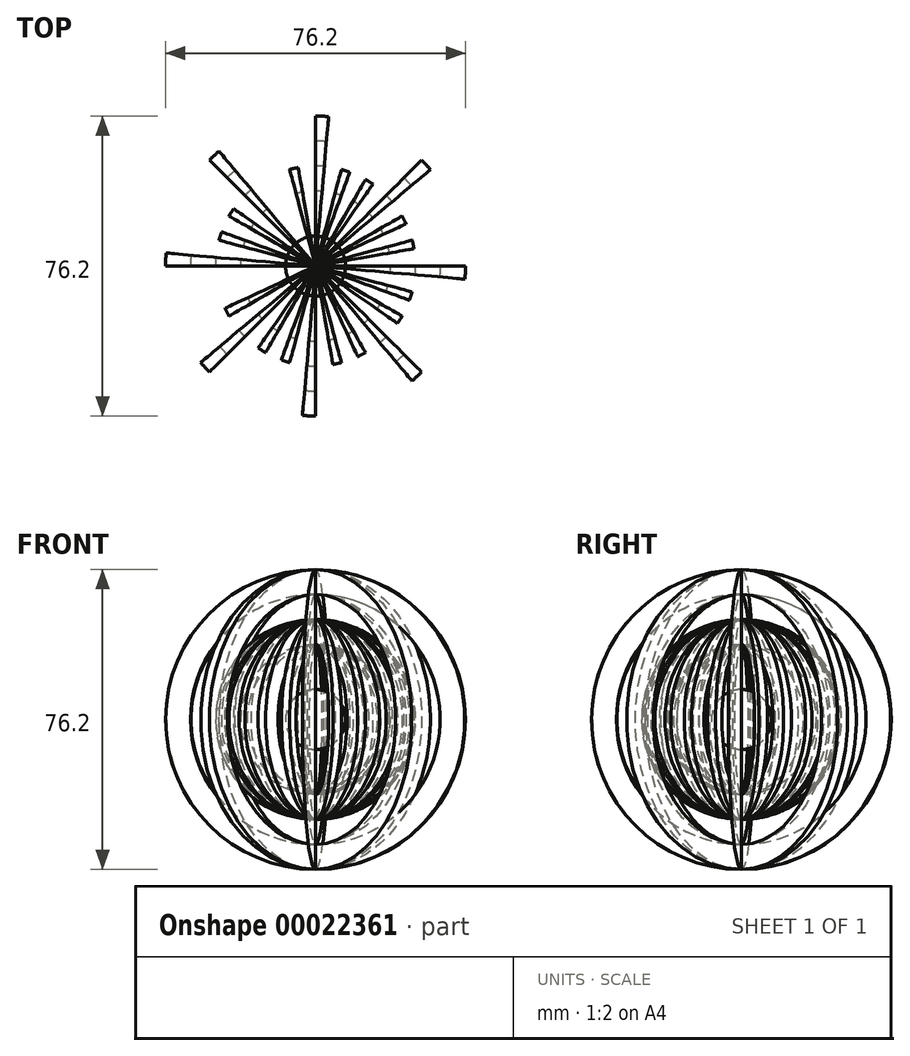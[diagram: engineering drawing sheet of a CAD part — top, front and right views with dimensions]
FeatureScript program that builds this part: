
annotation { "Feature Type Name" : "Feature", "Feature Type Description" : "" }
export const myFeature = defineFeature(function(context is Context, id is Id, definition is map)
    precondition{}
    {
        {
            var Q0;
            Q0=qCreatedBy(makeId("Right.planeOp"),FACE);
            var sketch = newSketch(context, id + "F0", { "sketchPlane" : qUnion([Q0])});
            skCircle(sketch, "E0", {"center": v(0, 0) * mm, "radius": 12.9 * mm});
            skCircle(sketch, "E1", {"center": v(0, 0) * mm, "radius": 6.75 * mm});
            skCircle(sketch, "E2", {"center": v(0, 0) * mm, "radius": 19.05 * mm});
            skCircle(sketch, "E3", {"center": v(0, 0) * mm, "radius": 25.4 * mm});
            skLineSegment(sketch, "E4", {"start": v(0, 49.46) * mm, "end": v(0, -44.6) * mm});
            skCircle(sketch, "E5", {"center": v(0, 0) * mm, "radius": 30.75 * mm});
            skLineSegment(sketch, "E6", {"start": v(0, 49.46) * mm, "end": v(0, 76.29) * mm, "construction": true});
            skLineSegment(sketch, "E7", {"start": v(0, 76.29) * mm, "end": v(7.81, 69.76) * mm, "construction": true});
            skLineSegment(sketch, "E8", {"start": v(-75.09, 75.98) * mm, "end": v(75.64, 76.29) * mm});
            skSolve(sketch);
        }
        {
            var Q0;
            {var subQ0=sQuery(id+"F0.wireOp",EDGE,"E4");var subQ1=sQuery(id+"F0.wireOp",EDGE,"E1");var subQ3=makeQuery(id+"F0.imprint","INTERSECT",VERTEX,{"disambiguationData":[OD(0.0)],"derivedFrom":[subQ1,subQ0]});Q0=makeQuery(id+"F0.imprint","IMPRINT",FACE,{"disambiguationData":[TD([[makeQuery(id+"F0.imprint","IMPRINT",EDGE,{"disambiguationData":[TD([[subQ3,1.0]])],"derivedFrom":subQ1}),1.0]])]});}
            var Q1;
            Q1=sQuery(id+"F0.wireOp",EDGE,"E4");
            revolve(context, id + "F1", {"entities" : qUnion([Q0]), "axis" : qUnion([Q1]), "revolveType" : RevolveType.FULL});
        }
        {
            var Q0;
            {var subQ0=sQuery(id+"F0.wireOp",EDGE,"E4");var subQ3=sQuery(id+"F0.wireOp",EDGE,"E2");var subQ6=makeQuery(id+"F0.imprint","INTERSECT",VERTEX,{"disambiguationData":[OD(0.0)],"derivedFrom":[subQ3,subQ0]});Q0=makeQuery(id+"F0.imprint","IMPRINT",FACE,{"disambiguationData":[TD([[makeQuery(id+"F0.imprint","IMPRINT",EDGE,{"disambiguationData":[TD([[subQ6,1.0]])],"derivedFrom":subQ3}),-1.0]])]});}
            var Q1;
            Q1=sQuery(id+"F0.wireOp",EDGE,"E4");
            revolve(context, id + "F2", {"entities" : qUnion([Q0]), "axis" : qUnion([Q1]), "revolveType" : RevolveType.ONE_DIRECTION, "angle" : 5 * degree});
        }
        {
            var Q0;
            Q0=qCreatedBy(makeId("Front.planeOp"),FACE);
            var sketch = newSketch(context, id + "F3", { "sketchPlane" : qUnion([Q0])});
            skCircle(sketch, "E9", {"center": v(0, 0) * mm, "radius": 25.4 * mm});
            skCircle(sketch, "E10", {"center": v(0, 0) * mm, "radius": 19.05 * mm});
            skLineSegment(sketch, "E11", {"start": v(0, 49.68) * mm, "end": v(0, -45.03) * mm});
            skLineSegment(sketch, "E12", {"start": v(77.84, 77.44) * mm, "end": v(-74.78, 77.44) * mm});
            skSolve(sketch);
        }
        {
            var Q0;
            {var subQ0=sQuery(id+"F3.wireOp",EDGE,"E11");var subQ3=sQuery(id+"F3.wireOp",EDGE,"E9");var subQ6=makeQuery(id+"F3.imprint","INTERSECT",VERTEX,{"disambiguationData":[OD(0.0)],"derivedFrom":[subQ3,subQ0]});Q0=makeQuery(id+"F3.imprint","IMPRINT",FACE,{"disambiguationData":[TD([[makeQuery(id+"F3.imprint","IMPRINT",EDGE,{"disambiguationData":[TD([[subQ6,-1.0]])],"derivedFrom":subQ3}),1.0]])]});}
            var Q1;
            Q1=sQuery(id+"F3.wireOp",EDGE,"E11");
            revolve(context, id + "F4", {"entities" : qUnion([Q0]), "axis" : qUnion([Q1]), "revolveType" : RevolveType.ONE_DIRECTION, "angle" : 5 * degree});
        }
        {
            var Q0;
            {var subQ0=sQuery(id+"F3.wireOp",EDGE,"E11");var subQ3=sQuery(id+"F3.wireOp",EDGE,"E9");var subQ6=makeQuery(id+"F3.imprint","INTERSECT",VERTEX,{"disambiguationData":[OD(0.0)],"derivedFrom":[subQ3,subQ0]});Q0=makeQuery(id+"F3.imprint","IMPRINT",FACE,{"disambiguationData":[TD([[makeQuery(id+"F3.imprint","IMPRINT",EDGE,{"disambiguationData":[TD([[subQ6,1.0]])],"derivedFrom":subQ3}),1.0]])]});}
            var Q1;
            Q1=sQuery(id+"F3.wireOp",EDGE,"E11");
            revolve(context, id + "F5", {"entities" : qUnion([Q0]), "axis" : qUnion([Q1]), "revolveType" : RevolveType.ONE_DIRECTION, "angle" : 5 * degree});
        }
        {
            var Q0;
            Q0=sQuery(id+"F3.wireOp",EDGE,"E11");
            cPlane(context, id + "F6", {"entities" : qUnion([Q0]), "cplaneType" : CPlaneType.LINE_ANGLE, "offset" : 152.4 * mm, "angle" : 135 * degree, "width" : 152.4 * mm, "height" : 152.4 * mm});
        }
        {
            var Q0;
            Q0=qCreatedBy(id+"F6.planeOp",FACE);
            var sketch = newSketch(context, id + "F7", { "sketchPlane" : qUnion([Q0])});
            skCircle(sketch, "E13", {"center": v(0, 0) * mm, "radius": 25.4 * mm});
            skCircle(sketch, "E14", {"center": v(0, 0) * mm, "radius": 19.05 * mm});
            skLineSegment(sketch, "E15", {"start": v(0, 49) * mm, "end": v(0, -46.81) * mm});
            skSolve(sketch);
        }
        {
            var Q0;
            {var subQ0=sQuery(id+"F7.wireOp",EDGE,"E15");var subQ3=sQuery(id+"F7.wireOp",EDGE,"E13");var subQ6=makeQuery(id+"F7.imprint","INTERSECT",VERTEX,{"disambiguationData":[OD(0.0)],"derivedFrom":[subQ3,subQ0]});Q0=makeQuery(id+"F7.imprint","IMPRINT",FACE,{"disambiguationData":[TD([[makeQuery(id+"F7.imprint","IMPRINT",EDGE,{"disambiguationData":[TD([[subQ6,1.0]])],"derivedFrom":subQ3}),1.0]])]});}
            var Q1;
            Q1=sQuery(id+"F7.wireOp",EDGE,"E15");
            revolve(context, id + "F8", {"entities" : qUnion([Q0]), "axis" : qUnion([Q1]), "revolveType" : RevolveType.ONE_DIRECTION, "angle" : 5 * degree});
        }
        {
            var Q0;
            {var subQ0=sQuery(id+"F7.wireOp",EDGE,"E15");var subQ3=sQuery(id+"F7.wireOp",EDGE,"E13");var subQ6=makeQuery(id+"F7.imprint","INTERSECT",VERTEX,{"disambiguationData":[OD(0.0)],"derivedFrom":[subQ3,subQ0]});Q0=makeQuery(id+"F7.imprint","IMPRINT",FACE,{"disambiguationData":[TD([[makeQuery(id+"F7.imprint","IMPRINT",EDGE,{"disambiguationData":[TD([[subQ6,-1.0]])],"derivedFrom":subQ3}),1.0]])]});}
            var Q1;
            Q1=sQuery(id+"F7.wireOp",EDGE,"E15");
            revolve(context, id + "F9", {"entities" : qUnion([Q0]), "axis" : qUnion([Q1]), "revolveType" : RevolveType.ONE_DIRECTION, "angle" : 5 * degree});
        }
        {
            var Q0;
            Q0=sQuery(id+"F7.wireOp",EDGE,"E15");
            cPlane(context, id + "F10", {"entities" : qUnion([Q0]), "cplaneType" : CPlaneType.LINE_ANGLE, "offset" : 152.4 * mm, "angle" : 45 * degree, "width" : 152.4 * mm, "height" : 152.4 * mm});
        }
        {
            var Q0;
            Q0=qCreatedBy(id+"F10.planeOp",FACE);
            var sketch = newSketch(context, id + "F11", { "sketchPlane" : qUnion([Q0])});
            skCircle(sketch, "E16", {"center": v(0, 0) * mm, "radius": 19.05 * mm});
            skLineSegment(sketch, "E17", {"start": v(0, 49.08) * mm, "end": v(0, -50.96) * mm});
            skCircle(sketch, "E18", {"center": v(0, 0) * mm, "radius": 25.4 * mm});
            skSolve(sketch);
        }
        {
            var Q0;
            {var subQ1=sQuery(id+"F11.wireOp",EDGE,"E17");var subQ4=sQuery(id+"F11.wireOp",EDGE,"E16");var subQ6=makeQuery(id+"F11.imprint","INTERSECT",VERTEX,{"disambiguationData":[OD(0.0)],"derivedFrom":[subQ4,subQ1]});Q0=makeQuery(id+"F11.imprint","IMPRINT",FACE,{"disambiguationData":[TD([[makeQuery(id+"F11.imprint","IMPRINT",EDGE,{"disambiguationData":[TD([[subQ6,1.0]])],"derivedFrom":subQ4}),-1.0]])]});}
            var Q1;
            Q1=sQuery(id+"F11.wireOp",EDGE,"E17");
            revolve(context, id + "F12", {"entities" : qUnion([Q0]), "axis" : qUnion([Q1]), "revolveType" : RevolveType.ONE_DIRECTION, "angle" : 5 * degree});
        }
        {
            var Q0;
            {var subQ0=sQuery(id+"F11.wireOp",EDGE,"E17");var subQ1=sQuery(id+"F11.wireOp",EDGE,"E16");var subQ6=makeQuery(id+"F11.imprint","INTERSECT",VERTEX,{"disambiguationData":[OD(0.0)],"derivedFrom":[subQ1,subQ0]});Q0=makeQuery(id+"F11.imprint","IMPRINT",FACE,{"disambiguationData":[TD([[makeQuery(id+"F11.imprint","IMPRINT",EDGE,{"disambiguationData":[TD([[subQ6,-1.0]])],"derivedFrom":subQ1}),-1.0]])]});}
            var Q1;
            Q1=sQuery(id+"F11.wireOp",EDGE,"E17");
            revolve(context, id + "F13", {"entities" : qUnion([Q0]), "axis" : qUnion([Q1]), "revolveType" : RevolveType.ONE_DIRECTION, "angle" : 5 * degree});
        }
        {
            var Q0;
            Q0=sQuery(id+"F11.wireOp",EDGE,"E17");
            cPlane(context, id + "F14", {"entities" : qUnion([Q0]), "cplaneType" : CPlaneType.LINE_ANGLE, "offset" : 152.4 * mm, "angle" : 15 * degree, "width" : 152.4 * mm, "height" : 152.4 * mm});
        }
        {
            var Q0;
            Q0=qCreatedBy(id+"F14.planeOp",FACE);
            var sketch = newSketch(context, id + "F15", { "sketchPlane" : qUnion([Q0])});
            skArc(sketch, "E19", {"start": v(0, 25.4) * mm, "mid": v(-25.4, 0) * mm, "end": v(0, -25.4) * mm});
            skArc(sketch, "E20", {"start": v(0, 19.05) * mm, "mid": v(-19.05, 0) * mm, "end": v(0, -19.05) * mm});
            skLineSegment(sketch, "E21", {"start": v(0, 47.4) * mm, "end": v(0, -52.09) * mm});
            skSolve(sketch);
        }
        {
            var Q0;
            {var subQ2=sQuery(id+"F15.wireOp",EDGE,"E19");Q0=makeQuery(id+"F15.imprint","IMPRINT",FACE,{"disambiguationData":[TD([[makeQuery(id+"F15.imprint","IMPRINT",EDGE,{"derivedFrom":subQ2}),1.0]])]});}
            var Q1;
            Q1=sQuery(id+"F15.wireOp",EDGE,"E21");
            revolve(context, id + "F16", {"entities" : qUnion([Q0]), "axis" : qUnion([Q1]), "revolveType" : RevolveType.ONE_DIRECTION, "angle" : 5 * degree});
        }
        {
            var Q0;
            Q0=qCreatedBy(id+"F14.planeOp",FACE);
            var sketch = newSketch(context, id + "F17", { "sketchPlane" : qUnion([Q0])});
            skArc(sketch, "E22", {"start": v(0, -25.4) * mm, "mid": v(25.4, 0) * mm, "end": v(0, 25.4) * mm});
            skArc(sketch, "E23", {"start": v(0, -19.05) * mm, "mid": v(19.05, 0) * mm, "end": v(0, 19.05) * mm});
            skLineSegment(sketch, "E24", {"start": v(0, 48.59) * mm, "end": v(0, -48.7) * mm});
            skSolve(sketch);
        }
        {
            var Q0;
            {var subQ2=sQuery(id+"F17.wireOp",EDGE,"E22");Q0=makeQuery(id+"F17.imprint","IMPRINT",FACE,{"disambiguationData":[TD([[makeQuery(id+"F17.imprint","IMPRINT",EDGE,{"derivedFrom":subQ2}),1.0]])]});}
            var Q1;
            Q1=sQuery(id+"F17.wireOp",EDGE,"E24");
            revolve(context, id + "F18", {"entities" : qUnion([Q0]), "axis" : qUnion([Q1]), "revolveType" : RevolveType.ONE_DIRECTION, "angle" : 5 * degree});
        }
        {
            var Q0;
            Q0=sQuery(id+"F11.wireOp",EDGE,"E17");
            cPlane(context, id + "F19", {"entities" : qUnion([Q0]), "cplaneType" : CPlaneType.LINE_ANGLE, "offset" : 152.4 * mm, "angle" : 30 * degree, "width" : 152.4 * mm, "height" : 152.4 * mm});
        }
        {
            var Q0;
            Q0=qCreatedBy(id+"F19.planeOp",FACE);
            var sketch = newSketch(context, id + "F20", { "sketchPlane" : qUnion([Q0])});
            skArc(sketch, "E25", {"start": v(0, -25.4) * mm, "mid": v(25.4, 0) * mm, "end": v(0, 25.4) * mm});
            skArc(sketch, "E26", {"start": v(0, -19.05) * mm, "mid": v(19.05, 0) * mm, "end": v(0, 19.05) * mm});
            skLineSegment(sketch, "E27", {"start": v(0, 48.62) * mm, "end": v(0, -52.83) * mm});
            skSolve(sketch);
        }
        {
            var Q0;
            {var subQ2=sQuery(id+"F20.wireOp",EDGE,"E25");Q0=makeQuery(id+"F20.imprint","IMPRINT",FACE,{"disambiguationData":[TD([[makeQuery(id+"F20.imprint","IMPRINT",EDGE,{"derivedFrom":subQ2}),1.0]])]});}
            var Q1;
            Q1=sQuery(id+"F20.wireOp",EDGE,"E27");
            revolve(context, id + "F21", {"operationType" : NewBodyOperationType.ADD, "entities" : qUnion([Q0]), "axis" : qUnion([Q1]), "revolveType" : RevolveType.ONE_DIRECTION, "angle" : 5 * degree});
        }
        {
            var Q0;
            Q0=qCreatedBy(id+"F19.planeOp",FACE);
            var sketch = newSketch(context, id + "F22", { "sketchPlane" : qUnion([Q0])});
            skArc(sketch, "E28", {"start": v(0, 25.4) * mm, "mid": v(-25.4, 0) * mm, "end": v(0, -25.4) * mm});
            skArc(sketch, "E29", {"start": v(0, 19.05) * mm, "mid": v(-19.05, 0) * mm, "end": v(0, -19.05) * mm});
            skLineSegment(sketch, "E30", {"start": v(0, 50.56) * mm, "end": v(0, -52.17) * mm});
            skSolve(sketch);
        }
        {
            var Q0;
            {var subQ2=sQuery(id+"F22.wireOp",EDGE,"E28");Q0=makeQuery(id+"F22.imprint","IMPRINT",FACE,{"disambiguationData":[TD([[makeQuery(id+"F22.imprint","IMPRINT",EDGE,{"derivedFrom":subQ2}),1.0]])]});}
            var Q1;
            Q1=sQuery(id+"F22.wireOp",EDGE,"E30");
            revolve(context, id + "F23", {"operationType" : NewBodyOperationType.ADD, "entities" : qUnion([Q0]), "axis" : qUnion([Q1]), "revolveType" : RevolveType.ONE_DIRECTION, "angle" : 5 * degree});
        }
        {
            var Q0;
            Q0=sQuery(id+"F11.wireOp",EDGE,"E17");
            cPlane(context, id + "F24", {"entities" : qUnion([Q0]), "cplaneType" : CPlaneType.LINE_ANGLE, "offset" : 152.4 * mm, "angle" : 60 * degree, "width" : 152.4 * mm, "height" : 152.4 * mm});
        }
        {
            var Q0;
            Q0=qCreatedBy(id+"F24.planeOp",FACE);
            var sketch = newSketch(context, id + "F25", { "sketchPlane" : qUnion([Q0])});
            skCircle(sketch, "E31", {"center": v(0, 0) * mm, "radius": 25.4 * mm});
            skCircle(sketch, "E32", {"center": v(0, 0) * mm, "radius": 19.05 * mm});
            skLineSegment(sketch, "E33", {"start": v(0, 47.75) * mm, "end": v(0, -47.16) * mm});
            skSolve(sketch);
        }
        {
            var Q0;
            {var subQ0=sQuery(id+"F25.wireOp",EDGE,"E33");var subQ3=sQuery(id+"F25.wireOp",EDGE,"E31");var subQ6=makeQuery(id+"F25.imprint","INTERSECT",VERTEX,{"disambiguationData":[OD(0.0)],"derivedFrom":[subQ3,subQ0]});Q0=makeQuery(id+"F25.imprint","IMPRINT",FACE,{"disambiguationData":[TD([[makeQuery(id+"F25.imprint","IMPRINT",EDGE,{"disambiguationData":[TD([[subQ6,1.0]])],"derivedFrom":subQ3}),1.0]])]});}
            var Q1;
            Q1=sQuery(id+"F25.wireOp",EDGE,"E33");
            revolve(context, id + "F26", {"operationType" : NewBodyOperationType.ADD, "entities" : qUnion([Q0]), "axis" : qUnion([Q1]), "revolveType" : RevolveType.ONE_DIRECTION, "angle" : 5 * degree});
        }
        {
            var Q0;
            {var subQ0=sQuery(id+"F25.wireOp",EDGE,"E33");var subQ3=sQuery(id+"F25.wireOp",EDGE,"E31");var subQ6=makeQuery(id+"F25.imprint","INTERSECT",VERTEX,{"disambiguationData":[OD(0.0)],"derivedFrom":[subQ3,subQ0]});Q0=makeQuery(id+"F25.imprint","IMPRINT",FACE,{"disambiguationData":[TD([[makeQuery(id+"F25.imprint","IMPRINT",EDGE,{"disambiguationData":[TD([[subQ6,-1.0]])],"derivedFrom":subQ3}),1.0]])]});}
            var Q1;
            Q1=sQuery(id+"F25.wireOp",EDGE,"E33");
            revolve(context, id + "F27", {"entities" : qUnion([Q0]), "axis" : qUnion([Q1]), "revolveType" : RevolveType.ONE_DIRECTION, "angle" : 5 * degree});
        }
        {
            var Q0;
            Q0=sQuery(id+"F25.wireOp",EDGE,"E33");
            cPlane(context, id + "F28", {"entities" : qUnion([Q0]), "cplaneType" : CPlaneType.LINE_ANGLE, "offset" : 152.4 * mm, "angle" : 75 * degree, "width" : 152.4 * mm, "height" : 152.4 * mm});
        }
        {
            var Q0;
            Q0=qCreatedBy(id+"F28.planeOp",FACE);
            var sketch = newSketch(context, id + "F29", { "sketchPlane" : qUnion([Q0])});
            skCircle(sketch, "E34", {"center": v(0, 0) * mm, "radius": 25.4 * mm});
            skCircle(sketch, "E35", {"center": v(0, 0) * mm, "radius": 19.05 * mm});
            skLineSegment(sketch, "E36", {"start": v(0, 25.4) * mm, "end": v(0, -25.4) * mm});
            skLineSegment(sketch, "E37", {"start": v(0, 39.45) * mm, "end": v(0, -34.84) * mm});
            skSolve(sketch);
        }
        {
            var Q0;
            {var subQ0=sQuery(id+"F29.wireOp",EDGE,"E37");var subQ3=sQuery(id+"F29.wireOp",EDGE,"E34");var subQ6=makeQuery(id+"F29.imprint","INTERSECT",VERTEX,{"disambiguationData":[OD(0.0)],"derivedFrom":[subQ3,subQ0]});Q0=makeQuery(id+"F29.imprint","IMPRINT",FACE,{"disambiguationData":[TD([[makeQuery(id+"F29.imprint","IMPRINT",EDGE,{"disambiguationData":[TD([[subQ6,1.0]])],"derivedFrom":subQ3}),1.0]])]});}
            var Q1;
            Q1=sQuery(id+"F29.wireOp",EDGE,"E36");
            revolve(context, id + "F30", {"operationType" : NewBodyOperationType.ADD, "entities" : qUnion([Q0]), "axis" : qUnion([Q1]), "revolveType" : RevolveType.ONE_DIRECTION, "angle" : 5 * degree});
        }
        {
            var Q0;
            Q0=qCreatedBy(id+"F28.planeOp",FACE);
            var sketch = newSketch(context, id + "F31", { "sketchPlane" : qUnion([Q0])});
            skArc(sketch, "E38", {"start": v(0, 25.4) * mm, "mid": v(-25.4, 0) * mm, "end": v(0, -25.4) * mm});
            skArc(sketch, "E39", {"start": v(0, 19.05) * mm, "mid": v(-19.05, 0) * mm, "end": v(0, -19.05) * mm});
            skLineSegment(sketch, "E40", {"start": v(0, 39.76) * mm, "end": v(0, -34.84) * mm});
            skSolve(sketch);
        }
        {
            var Q0;
            {var subQ2=sQuery(id+"F31.wireOp",EDGE,"E38");Q0=makeQuery(id+"F31.imprint","IMPRINT",FACE,{"disambiguationData":[TD([[makeQuery(id+"F31.imprint","IMPRINT",EDGE,{"derivedFrom":subQ2}),1.0]])]});}
            var Q1;
            Q1=sQuery(id+"F31.wireOp",EDGE,"E40");
            revolve(context, id + "F32", {"operationType" : NewBodyOperationType.ADD, "entities" : qUnion([Q0]), "axis" : qUnion([Q1]), "revolveType" : RevolveType.ONE_DIRECTION, "angle" : 5 * degree});
        }
        {
            var Q0;
            Q0=sQuery(id+"F29.wireOp",EDGE,"E37");
            cPlane(context, id + "F33", {"entities" : qUnion([Q0]), "cplaneType" : CPlaneType.LINE_ANGLE, "offset" : 152.4 * mm, "angle" : 105 * degree, "width" : 152.4 * mm, "height" : 152.4 * mm});
        }
        {
            var Q0;
            Q0=qCreatedBy(id+"F33.planeOp",FACE);
            var sketch = newSketch(context, id + "F34", { "sketchPlane" : qUnion([Q0])});
            skCircle(sketch, "E41", {"center": v(0, 0) * mm, "radius": 25.4 * mm});
            skCircle(sketch, "E42", {"center": v(0, 0) * mm, "radius": 19.05 * mm});
            skLineSegment(sketch, "E43", {"start": v(0, 30.33) * mm, "end": v(0, -31.57) * mm});
            skSolve(sketch);
        }
        {
            var Q0;
            {var subQ0=sQuery(id+"F34.wireOp",EDGE,"E43");var subQ3=sQuery(id+"F34.wireOp",EDGE,"E41");var subQ6=makeQuery(id+"F34.imprint","INTERSECT",VERTEX,{"disambiguationData":[OD(0.0)],"derivedFrom":[subQ3,subQ0]});Q0=makeQuery(id+"F34.imprint","IMPRINT",FACE,{"disambiguationData":[TD([[makeQuery(id+"F34.imprint","IMPRINT",EDGE,{"disambiguationData":[TD([[subQ6,1.0]])],"derivedFrom":subQ3}),1.0]])]});}
            var Q1;
            Q1=sQuery(id+"F34.wireOp",EDGE,"E43");
            revolve(context, id + "F35", {"entities" : qUnion([Q0]), "axis" : qUnion([Q1]), "revolveType" : RevolveType.ONE_DIRECTION, "angle" : 5 * degree});
        }
        {
            var Q0;
            {var subQ0=sQuery(id+"F34.wireOp",EDGE,"E43");var subQ3=sQuery(id+"F34.wireOp",EDGE,"E41");var subQ6=makeQuery(id+"F34.imprint","INTERSECT",VERTEX,{"disambiguationData":[OD(0.0)],"derivedFrom":[subQ3,subQ0]});Q0=makeQuery(id+"F34.imprint","IMPRINT",FACE,{"disambiguationData":[TD([[makeQuery(id+"F34.imprint","IMPRINT",EDGE,{"disambiguationData":[TD([[subQ6,-1.0]])],"derivedFrom":subQ3}),1.0]])]});}
            var Q1;
            Q1=sQuery(id+"F34.wireOp",EDGE,"E43");
            revolve(context, id + "F36", {"operationType" : NewBodyOperationType.ADD, "entities" : qUnion([Q0]), "axis" : qUnion([Q1]), "revolveType" : RevolveType.ONE_DIRECTION, "angle" : 5 * degree});
        }
        {
            var Q0;
            Q0=sQuery(id+"F34.wireOp",EDGE,"E43");
            cPlane(context, id + "F37", {"entities" : qUnion([Q0]), "cplaneType" : CPlaneType.LINE_ANGLE, "offset" : 304.8 * mm, "angle" : 120 * degree, "width" : 152.4 * mm, "height" : 152.4 * mm});
        }
        {
            var Q0;
            Q0=qCreatedBy(id+"F37.planeOp",FACE);
            var sketch = newSketch(context, id + "F38", { "sketchPlane" : qUnion([Q0])});
            skCircle(sketch, "E44", {"center": v(0, 0) * mm, "radius": 25.4 * mm});
            skCircle(sketch, "E45", {"center": v(0, 0) * mm, "radius": 19.05 * mm});
            skLineSegment(sketch, "E46", {"start": v(0, 30.85) * mm, "end": v(0, -32.35) * mm});
            skSolve(sketch);
        }
        {
            var Q0;
            {var subQ0=sQuery(id+"F38.wireOp",EDGE,"E46");var subQ3=sQuery(id+"F38.wireOp",EDGE,"E44");var subQ6=makeQuery(id+"F38.imprint","INTERSECT",VERTEX,{"disambiguationData":[OD(0.0)],"derivedFrom":[subQ3,subQ0]});Q0=makeQuery(id+"F38.imprint","IMPRINT",FACE,{"disambiguationData":[TD([[makeQuery(id+"F38.imprint","IMPRINT",EDGE,{"disambiguationData":[TD([[subQ6,1.0]])],"derivedFrom":subQ3}),1.0]])]});}
            var Q1;
            Q1=sQuery(id+"F38.wireOp",EDGE,"E46");
            revolve(context, id + "F39", {"operationType" : NewBodyOperationType.ADD, "entities" : qUnion([Q0]), "axis" : qUnion([Q1]), "revolveType" : RevolveType.ONE_DIRECTION, "angle" : 5 * degree});
        }
        {
            var Q0;
            {var subQ0=sQuery(id+"F38.wireOp",EDGE,"E46");var subQ3=sQuery(id+"F38.wireOp",EDGE,"E44");var subQ6=makeQuery(id+"F38.imprint","INTERSECT",VERTEX,{"disambiguationData":[OD(0.0)],"derivedFrom":[subQ3,subQ0]});Q0=makeQuery(id+"F38.imprint","IMPRINT",FACE,{"disambiguationData":[TD([[makeQuery(id+"F38.imprint","IMPRINT",EDGE,{"disambiguationData":[TD([[subQ6,-1.0]])],"derivedFrom":subQ3}),1.0]])]});}
            var Q1;
            Q1=sQuery(id+"F38.wireOp",EDGE,"E46");
            revolve(context, id + "F40", {"operationType" : NewBodyOperationType.ADD, "entities" : qUnion([Q0]), "axis" : qUnion([Q1]), "revolveType" : RevolveType.ONE_DIRECTION, "angle" : 5 * degree});
        }
        {
            var Q0;
            Q0=sQuery(id+"F38.wireOp",EDGE,"E46");
            cPlane(context, id + "F41", {"entities" : qUnion([Q0]), "cplaneType" : CPlaneType.LINE_ANGLE, "offset" : 152.4 * mm, "angle" : 150 * degree, "width" : 152.4 * mm, "height" : 152.4 * mm});
        }
        {
            var Q0;
            Q0=qCreatedBy(id+"F41.planeOp",FACE);
            var sketch = newSketch(context, id + "F42", { "sketchPlane" : qUnion([Q0])});
            skArc(sketch, "E47", {"start": v(0, -25.4) * mm, "mid": v(25.4, 0) * mm, "end": v(0, 25.4) * mm});
            skArc(sketch, "E48", {"start": v(0, -19.05) * mm, "mid": v(19.05, 0) * mm, "end": v(0, 19.05) * mm});
            skLineSegment(sketch, "E49", {"start": v(0, 32.04) * mm, "end": v(0, -30.23) * mm});
            skCircle(sketch, "E50", {"center": v(0, 0) * mm, "radius": 25.4 * mm});
            skCircle(sketch, "E51", {"center": v(0, 0) * mm, "radius": 25.44 * mm});
            skCircle(sketch, "E52", {"center": v(0, 0) * mm, "radius": 19.05 * mm});
            skLineSegment(sketch, "E53", {"start": v(0, 27.78) * mm, "end": v(0, -30.23) * mm});
            skSolve(sketch);
        }
        {
            var Q0;
            {var subQ0=sQuery(id+"F42.wireOp",EDGE,"E53");var subQ3=sQuery(id+"F42.wireOp",EDGE,"E50");var subQ6=makeQuery(id+"F42.imprint","INTERSECT",VERTEX,{"disambiguationData":[OD(0.0)],"derivedFrom":[subQ3,subQ0]});Q0=makeQuery(id+"F42.imprint","IMPRINT",FACE,{"disambiguationData":[TD([[makeQuery(id+"F42.imprint","IMPRINT",EDGE,{"disambiguationData":[TD([[subQ6,1.0]])],"derivedFrom":subQ3}),1.0]])]});}
            var Q1;
            Q1=sQuery(id+"F42.wireOp",EDGE,"E49");
            revolve(context, id + "F43", {"operationType" : NewBodyOperationType.ADD, "entities" : qUnion([Q0]), "axis" : qUnion([Q1]), "revolveType" : RevolveType.ONE_DIRECTION, "angle" : 5 * degree});
        }
        {
            var Q0;
            Q0=sQuery(id+"F42.wireOp",EDGE,"E49");
            cPlane(context, id + "F44", {"entities" : qUnion([Q0]), "cplaneType" : CPlaneType.LINE_ANGLE, "offset" : 152.4 * mm, "angle" : 165 * degree, "width" : 152.4 * mm, "height" : 152.4 * mm});
        }
        {
            var Q0;
            Q0=qCreatedBy(id+"F44.planeOp",FACE);
            var sketch = newSketch(context, id + "F45", { "sketchPlane" : qUnion([Q0])});
            skCircle(sketch, "E54", {"center": v(0, 0) * mm, "radius": 25.4 * mm});
            skCircle(sketch, "E55", {"center": v(0, 0) * mm, "radius": 19.05 * mm});
            skLineSegment(sketch, "E56", {"start": v(0, 32.04) * mm, "end": v(0, -31.18) * mm});
            skSolve(sketch);
        }
        {
            var Q0;
            {var subQ0=sQuery(id+"F45.wireOp",EDGE,"E56");var subQ3=sQuery(id+"F45.wireOp",EDGE,"E54");var subQ6=makeQuery(id+"F45.imprint","INTERSECT",VERTEX,{"disambiguationData":[OD(0.0)],"derivedFrom":[subQ3,subQ0]});Q0=makeQuery(id+"F45.imprint","IMPRINT",FACE,{"disambiguationData":[TD([[makeQuery(id+"F45.imprint","IMPRINT",EDGE,{"disambiguationData":[TD([[subQ6,1.0]])],"derivedFrom":subQ3}),1.0]])]});}
            var Q1;
            Q1=sQuery(id+"F45.wireOp",EDGE,"E56");
            revolve(context, id + "F46", {"entities" : qUnion([Q0]), "axis" : qUnion([Q1]), "revolveType" : RevolveType.ONE_DIRECTION, "angle" : 5 * degree});
        }
        {
            var Q0;
            {var subQ0=sQuery(id+"F45.wireOp",EDGE,"E56");var subQ3=sQuery(id+"F45.wireOp",EDGE,"E54");var subQ6=makeQuery(id+"F45.imprint","INTERSECT",VERTEX,{"disambiguationData":[OD(0.0)],"derivedFrom":[subQ3,subQ0]});Q0=makeQuery(id+"F45.imprint","IMPRINT",FACE,{"disambiguationData":[TD([[makeQuery(id+"F45.imprint","IMPRINT",EDGE,{"disambiguationData":[TD([[subQ6,-1.0]])],"derivedFrom":subQ3}),1.0]])]});}
            var Q1;
            Q1=sQuery(id+"F45.wireOp",EDGE,"E56");
            revolve(context, id + "F47", {"entities" : qUnion([Q0]), "axis" : qUnion([Q1]), "revolveType" : RevolveType.ONE_DIRECTION, "angle" : 5 * degree});
        }
        {
            var Q0;
            Q0=qCreatedBy(makeId("Front.planeOp"),FACE);
            var sketch = newSketch(context, id + "F48", { "sketchPlane" : qUnion([Q0])});
            skArc(sketch, "E57", {"start": v(0, -7.62) * mm, "mid": v(7.62, 0) * mm, "end": v(0, 7.62) * mm});
            skLineSegment(sketch, "E58", {"start": v(0, 10.13) * mm, "end": v(0, -9.26) * mm});
            skSolve(sketch);
        }
        {
            var Q0;
            Q0 = qSketchRegion(id + "F48", true);
            var Q1;
            Q1=sQuery(id+"F45.wireOp",EDGE,"E56");
            revolve(context, id + "F49", {"entities" : qUnion([Q0]), "axis" : qUnion([Q1]), "revolveType" : RevolveType.FULL});
        }
        {
            var Q0;
            Q0=qCreatedBy(makeId("Front.planeOp"),FACE);
            var sketch = newSketch(context, id + "F50", { "sketchPlane" : qUnion([Q0])});
            skCircle(sketch, "E59", {"center": v(0, 0) * mm, "radius": 38.1 * mm});
            skCircle(sketch, "E60", {"center": v(0, 0) * mm, "radius": 31.75 * mm});
            skLineSegment(sketch, "E61", {"start": v(0, 44.65) * mm, "end": v(0, -44.4) * mm});
            skSolve(sketch);
        }
        {
            var Q0;
            {var subQ0=sQuery(id+"F50.wireOp",EDGE,"E61");var subQ3=sQuery(id+"F50.wireOp",EDGE,"E59");var subQ6=makeQuery(id+"F50.imprint","INTERSECT",VERTEX,{"disambiguationData":[OD(0.0)],"derivedFrom":[subQ3,subQ0]});Q0=makeQuery(id+"F50.imprint","IMPRINT",FACE,{"disambiguationData":[TD([[makeQuery(id+"F50.imprint","IMPRINT",EDGE,{"disambiguationData":[TD([[subQ6,-1.0]])],"derivedFrom":subQ3}),1.0]])]});}
            var Q1;
            Q1=sQuery(id+"F50.wireOp",EDGE,"E61");
            revolve(context, id + "F51", {"entities" : qUnion([Q0]), "axis" : qUnion([Q1]), "revolveType" : RevolveType.ONE_DIRECTION, "angle" : 5 * degree});
        }
        {
            var Q0;
            {var subQ0=sQuery(id+"F50.wireOp",EDGE,"E61");var subQ3=sQuery(id+"F50.wireOp",EDGE,"E59");var subQ6=makeQuery(id+"F50.imprint","INTERSECT",VERTEX,{"disambiguationData":[OD(0.0)],"derivedFrom":[subQ3,subQ0]});Q0=makeQuery(id+"F50.imprint","IMPRINT",FACE,{"disambiguationData":[TD([[makeQuery(id+"F50.imprint","IMPRINT",EDGE,{"disambiguationData":[TD([[subQ6,1.0]])],"derivedFrom":subQ3}),1.0]])]});}
            var Q1;
            Q1=sQuery(id+"F50.wireOp",EDGE,"E61");
            revolve(context, id + "F52", {"entities" : qUnion([Q0]), "axis" : qUnion([Q1]), "revolveType" : RevolveType.ONE_DIRECTION, "angle" : 5 * degree});
        }
        {
            var Q0;
            Q0=qCreatedBy(makeId("Right.planeOp"),FACE);
            var sketch = newSketch(context, id + "F53", { "sketchPlane" : qUnion([Q0])});
            skCircle(sketch, "E62", {"center": v(0, 0) * mm, "radius": 38.1 * mm});
            skCircle(sketch, "E63", {"center": v(0, 0) * mm, "radius": 31.75 * mm});
            skLineSegment(sketch, "E64", {"start": v(0, 45.64) * mm, "end": v(0, -49.23) * mm});
            skSolve(sketch);
        }
        {
            var Q0;
            {var subQ0=sQuery(id+"F53.wireOp",EDGE,"E64");var subQ3=sQuery(id+"F53.wireOp",EDGE,"E62");var subQ6=makeQuery(id+"F53.imprint","INTERSECT",VERTEX,{"disambiguationData":[OD(0.0)],"derivedFrom":[subQ3,subQ0]});Q0=makeQuery(id+"F53.imprint","IMPRINT",FACE,{"disambiguationData":[TD([[makeQuery(id+"F53.imprint","IMPRINT",EDGE,{"disambiguationData":[TD([[subQ6,-1.0]])],"derivedFrom":subQ3}),1.0]])]});}
            var Q1;
            Q1=sQuery(id+"F53.wireOp",EDGE,"E64");
            revolve(context, id + "F54", {"entities" : qUnion([Q0]), "axis" : qUnion([Q1]), "revolveType" : RevolveType.ONE_DIRECTION, "angle" : 5 * degree});
        }
        {
            var Q0;
            {var subQ0=sQuery(id+"F53.wireOp",EDGE,"E64");var subQ3=sQuery(id+"F53.wireOp",EDGE,"E62");var subQ6=makeQuery(id+"F53.imprint","INTERSECT",VERTEX,{"disambiguationData":[OD(0.0)],"derivedFrom":[subQ3,subQ0]});Q0=makeQuery(id+"F53.imprint","IMPRINT",FACE,{"disambiguationData":[TD([[makeQuery(id+"F53.imprint","IMPRINT",EDGE,{"disambiguationData":[TD([[subQ6,1.0]])],"derivedFrom":subQ3}),1.0]])]});}
            var Q1;
            Q1=sQuery(id+"F53.wireOp",EDGE,"E64");
            revolve(context, id + "F55", {"entities" : qUnion([Q0]), "axis" : qUnion([Q1]), "revolveType" : RevolveType.ONE_DIRECTION, "angle" : 5 * degree});
        }
        {
            var Q0;
            Q0=qCreatedBy(id+"F6.planeOp",FACE);
            var sketch = newSketch(context, id + "F56", { "sketchPlane" : qUnion([Q0])});
            skCircle(sketch, "E65", {"center": v(0, 0) * mm, "radius": 38.1 * mm});
            skCircle(sketch, "E66", {"center": v(0, 0) * mm, "radius": 31.75 * mm});
            skLineSegment(sketch, "E67", {"start": v(0, 45.64) * mm, "end": v(0, -50.22) * mm});
            skSolve(sketch);
        }
        {
            var Q0;
            {var subQ0=sQuery(id+"F56.wireOp",EDGE,"E67");var subQ3=sQuery(id+"F56.wireOp",EDGE,"E65");var subQ6=makeQuery(id+"F56.imprint","INTERSECT",VERTEX,{"disambiguationData":[OD(0.0)],"derivedFrom":[subQ3,subQ0]});Q0=makeQuery(id+"F56.imprint","IMPRINT",FACE,{"disambiguationData":[TD([[makeQuery(id+"F56.imprint","IMPRINT",EDGE,{"disambiguationData":[TD([[subQ6,1.0]])],"derivedFrom":subQ3}),1.0]])]});}
            var Q1;
            Q1=sQuery(id+"F56.wireOp",EDGE,"E67");
            revolve(context, id + "F57", {"entities" : qUnion([Q0]), "axis" : qUnion([Q1]), "revolveType" : RevolveType.ONE_DIRECTION, "angle" : 5 * degree});
        }
        {
            var Q0;
            {var subQ0=sQuery(id+"F56.wireOp",EDGE,"E67");var subQ3=sQuery(id+"F56.wireOp",EDGE,"E65");var subQ6=makeQuery(id+"F56.imprint","INTERSECT",VERTEX,{"disambiguationData":[OD(0.0)],"derivedFrom":[subQ3,subQ0]});Q0=makeQuery(id+"F56.imprint","IMPRINT",FACE,{"disambiguationData":[TD([[makeQuery(id+"F56.imprint","IMPRINT",EDGE,{"disambiguationData":[TD([[subQ6,-1.0]])],"derivedFrom":subQ3}),1.0]])]});}
            var Q1;
            Q1=sQuery(id+"F56.wireOp",EDGE,"E67");
            revolve(context, id + "F58", {"entities" : qUnion([Q0]), "axis" : qUnion([Q1]), "revolveType" : RevolveType.ONE_DIRECTION, "angle" : 5 * degree});
        }
        {
            var Q0;
            Q0=qCreatedBy(id+"F10.planeOp",FACE);
            var sketch = newSketch(context, id + "F59", { "sketchPlane" : qUnion([Q0])});
            skCircle(sketch, "E68", {"center": v(0, 0) * mm, "radius": 38.1 * mm});
            skCircle(sketch, "E69", {"center": v(0, 0) * mm, "radius": 31.75 * mm});
            skLineSegment(sketch, "E70", {"start": v(0, 45.4) * mm, "end": v(0, -47.36) * mm});
            skSolve(sketch);
        }
        {
            var Q0;
            {var subQ0=sQuery(id+"F59.wireOp",EDGE,"E70");var subQ3=sQuery(id+"F59.wireOp",EDGE,"E68");var subQ6=makeQuery(id+"F59.imprint","INTERSECT",VERTEX,{"disambiguationData":[OD(0.0)],"derivedFrom":[subQ3,subQ0]});Q0=makeQuery(id+"F59.imprint","IMPRINT",FACE,{"disambiguationData":[TD([[makeQuery(id+"F59.imprint","IMPRINT",EDGE,{"disambiguationData":[TD([[subQ6,1.0]])],"derivedFrom":subQ3}),1.0]])]});}
            var Q1;
            Q1=sQuery(id+"F59.wireOp",EDGE,"E70");
            revolve(context, id + "F60", {"entities" : qUnion([Q0]), "axis" : qUnion([Q1]), "revolveType" : RevolveType.ONE_DIRECTION, "angle" : 5 * degree});
        }
        {
            var Q0;
            {var subQ0=sQuery(id+"F59.wireOp",EDGE,"E70");var subQ3=sQuery(id+"F59.wireOp",EDGE,"E68");var subQ6=makeQuery(id+"F59.imprint","INTERSECT",VERTEX,{"disambiguationData":[OD(0.0)],"derivedFrom":[subQ3,subQ0]});Q0=makeQuery(id+"F59.imprint","IMPRINT",FACE,{"disambiguationData":[TD([[makeQuery(id+"F59.imprint","IMPRINT",EDGE,{"disambiguationData":[TD([[subQ6,-1.0]])],"derivedFrom":subQ3}),1.0]])]});}
            var Q1;
            Q1=sQuery(id+"F59.wireOp",EDGE,"E70");
            revolve(context, id + "F61", {"entities" : qUnion([Q0]), "axis" : qUnion([Q1]), "revolveType" : RevolveType.ONE_DIRECTION, "angle" : 5 * degree});
        }
        {
            var Q0;
            {var subQ0=sQuery(id+"F42.wireOp",EDGE,"E53");var subQ3=sQuery(id+"F42.wireOp",EDGE,"E50");var subQ6=makeQuery(id+"F42.imprint","INTERSECT",VERTEX,{"disambiguationData":[OD(0.0)],"derivedFrom":[subQ3,subQ0]});Q0=makeQuery(id+"F42.imprint","IMPRINT",FACE,{"disambiguationData":[TD([[makeQuery(id+"F42.imprint","IMPRINT",EDGE,{"disambiguationData":[TD([[subQ6,-1.0]])],"derivedFrom":subQ3}),1.0]])]});}
            var Q1;
            Q1=sQuery(id+"F42.wireOp",EDGE,"E53");
            revolve(context, id + "F62", {"entities" : qUnion([Q0]), "axis" : qUnion([Q1]), "revolveType" : RevolveType.ONE_DIRECTION, "angle" : 5 * degree});
        }
        {
            var Q0;
            {var subQ0=sQuery(id+"F42.wireOp",EDGE,"E53");var subQ3=sQuery(id+"F42.wireOp",EDGE,"E50");var subQ6=makeQuery(id+"F42.imprint","INTERSECT",VERTEX,{"disambiguationData":[OD(0.0)],"derivedFrom":[subQ3,subQ0]});Q0=makeQuery(id+"F42.imprint","IMPRINT",FACE,{"disambiguationData":[TD([[makeQuery(id+"F42.imprint","IMPRINT",EDGE,{"disambiguationData":[TD([[subQ6,1.0]])],"derivedFrom":subQ3}),1.0]])]});}
            var Q1;
            Q1=sQuery(id+"F42.wireOp",EDGE,"E53");
            revolve(context, id + "F63", {"entities" : qUnion([Q0]), "axis" : qUnion([Q1]), "revolveType" : RevolveType.ONE_DIRECTION, "angle" : 5 * degree});
        }
        {
            var Q0;
            {var subQ0=sQuery(id+"F0.wireOp",EDGE,"E4");var subQ3=sQuery(id+"F0.wireOp",EDGE,"E2");var subQ6=makeQuery(id+"F0.imprint","INTERSECT",VERTEX,{"disambiguationData":[OD(0.0)],"derivedFrom":[subQ3,subQ0]});Q0=makeQuery(id+"F0.imprint","IMPRINT",FACE,{"disambiguationData":[TD([[makeQuery(id+"F0.imprint","IMPRINT",EDGE,{"disambiguationData":[TD([[subQ6,-1.0]])],"derivedFrom":subQ3}),-1.0]])]});}
            var Q1;
            Q1=sQuery(id+"F0.wireOp",EDGE,"E4");
            revolve(context, id + "F64", {"entities" : qUnion([Q0]), "axis" : qUnion([Q1]), "revolveType" : RevolveType.ONE_DIRECTION, "angle" : 5 * degree});
        }
        {
            var Q0;
            Q0=makeQuery(id+"F1.opRevolve","SWEPT_BODY",BODY,{"disambiguationData":[OSD([sQuery(id+"F0.wireOp",EDGE,"E1"),sQuery(id+"F0.wireOp",EDGE,"E4")])]});
            var Q1;
            Q1=makeQuery(id+"F2.opRevolve","SWEPT_BODY",BODY,{"disambiguationData":[OSD([sQuery(id+"F0.wireOp",EDGE,"E2"),sQuery(id+"F0.wireOp",EDGE,"E3"),sQuery(id+"F0.wireOp",EDGE,"E4")])]});
            var Q2;
            Q2=makeQuery(id+"F4.opRevolve","SWEPT_BODY",BODY,{"disambiguationData":[OSD([sQuery(id+"F3.wireOp",EDGE,"E9"),sQuery(id+"F3.wireOp",EDGE,"E10"),sQuery(id+"F3.wireOp",EDGE,"E11")])]});
            var Q3;
            Q3=makeQuery(id+"F5.opRevolve","SWEPT_BODY",BODY,{"disambiguationData":[OSD([sQuery(id+"F3.wireOp",EDGE,"E9"),sQuery(id+"F3.wireOp",EDGE,"E10"),sQuery(id+"F3.wireOp",EDGE,"E11")])]});
            var Q4;
            Q4=makeQuery(id+"F8.opRevolve","SWEPT_BODY",BODY,{"disambiguationData":[OSD([sQuery(id+"F7.wireOp",EDGE,"E13"),sQuery(id+"F7.wireOp",EDGE,"E14"),sQuery(id+"F7.wireOp",EDGE,"E15")])]});
            var Q5;
            Q5=makeQuery(id+"F9.opRevolve","SWEPT_BODY",BODY,{"disambiguationData":[OSD([sQuery(id+"F7.wireOp",EDGE,"E13"),sQuery(id+"F7.wireOp",EDGE,"E14"),sQuery(id+"F7.wireOp",EDGE,"E15")])]});
            var Q6;
            Q6=makeQuery(id+"F12.opRevolve","SWEPT_BODY",BODY,{"disambiguationData":[OSD([sQuery(id+"F11.wireOp",EDGE,"E16"),sQuery(id+"F11.wireOp",EDGE,"E17"),sQuery(id+"F11.wireOp",EDGE,"E18")])]});
            var Q7;
            Q7=makeQuery(id+"F13.opRevolve","SWEPT_BODY",BODY,{"disambiguationData":[OSD([sQuery(id+"F11.wireOp",EDGE,"E16"),sQuery(id+"F11.wireOp",EDGE,"E17"),sQuery(id+"F11.wireOp",EDGE,"E18")])]});
            var Q8;
            Q8=makeQuery(id+"F16.opRevolve","SWEPT_BODY",BODY,{"disambiguationData":[OSD([sQuery(id+"F15.wireOp",EDGE,"E19"),sQuery(id+"F15.wireOp",EDGE,"E20"),sQuery(id+"F15.wireOp",EDGE,"E21")])]});
            var Q9;
            Q9=makeQuery(id+"F18.opRevolve","SWEPT_BODY",BODY,{"disambiguationData":[OSD([sQuery(id+"F17.wireOp",EDGE,"E22"),sQuery(id+"F17.wireOp",EDGE,"E23"),sQuery(id+"F17.wireOp",EDGE,"E24")])]});
            var Q10;
            Q10=makeQuery(id+"F21.opRevolve","SWEPT_BODY",BODY,{"disambiguationData":[OSD([sQuery(id+"F20.wireOp",EDGE,"E25"),sQuery(id+"F20.wireOp",EDGE,"E26"),sQuery(id+"F20.wireOp",EDGE,"E27")])]});
            var Q11;
            Q11=makeQuery(id+"F23.opRevolve","SWEPT_BODY",BODY,{"disambiguationData":[OSD([sQuery(id+"F22.wireOp",EDGE,"E28"),sQuery(id+"F22.wireOp",EDGE,"E29"),sQuery(id+"F22.wireOp",EDGE,"E30")])]});
            var Q12;
            Q12=makeQuery(id+"F26.opRevolve","SWEPT_BODY",BODY,{"disambiguationData":[OSD([sQuery(id+"F25.wireOp",EDGE,"E31"),sQuery(id+"F25.wireOp",EDGE,"E32"),sQuery(id+"F25.wireOp",EDGE,"E33")])]});
            var Q13;
            Q13=makeQuery(id+"F27.opRevolve","SWEPT_BODY",BODY,{"disambiguationData":[OSD([sQuery(id+"F25.wireOp",EDGE,"E31"),sQuery(id+"F25.wireOp",EDGE,"E32"),sQuery(id+"F25.wireOp",EDGE,"E33")])]});
            var Q14;
            Q14=makeQuery(id+"F30.opRevolve","SWEPT_BODY",BODY,{"disambiguationData":[OSD([sQuery(id+"F29.wireOp",EDGE,"E34"),sQuery(id+"F29.wireOp",EDGE,"E35"),sQuery(id+"F29.wireOp",EDGE,"E37")])]});
            var Q15;
            Q15=makeQuery(id+"F32.opRevolve","SWEPT_BODY",BODY,{"disambiguationData":[OSD([sQuery(id+"F31.wireOp",EDGE,"E38"),sQuery(id+"F31.wireOp",EDGE,"E39"),sQuery(id+"F31.wireOp",EDGE,"E40")])]});
            var Q16;
            Q16=makeQuery(id+"F35.opRevolve","SWEPT_BODY",BODY,{"disambiguationData":[OSD([sQuery(id+"F34.wireOp",EDGE,"E41"),sQuery(id+"F34.wireOp",EDGE,"E42"),sQuery(id+"F34.wireOp",EDGE,"E43")])]});
            var Q17;
            Q17=makeQuery(id+"F36.opRevolve","SWEPT_BODY",BODY,{"disambiguationData":[OSD([sQuery(id+"F34.wireOp",EDGE,"E41"),sQuery(id+"F34.wireOp",EDGE,"E42"),sQuery(id+"F34.wireOp",EDGE,"E43")])]});
            var Q18;
            Q18=makeQuery(id+"F39.opRevolve","SWEPT_BODY",BODY,{"disambiguationData":[OSD([sQuery(id+"F38.wireOp",EDGE,"E44"),sQuery(id+"F38.wireOp",EDGE,"E45"),sQuery(id+"F38.wireOp",EDGE,"E46")])]});
            var Q19;
            Q19=makeQuery(id+"F40.opRevolve","SWEPT_BODY",BODY,{"disambiguationData":[OSD([sQuery(id+"F38.wireOp",EDGE,"E44"),sQuery(id+"F38.wireOp",EDGE,"E45"),sQuery(id+"F38.wireOp",EDGE,"E46")])]});
            var Q20;
            Q20=makeQuery(id+"F43.opRevolve","SWEPT_BODY",BODY,{"disambiguationData":[OSD([sQuery(id+"F42.wireOp",EDGE,"E50"),sQuery(id+"F42.wireOp",EDGE,"E52"),sQuery(id+"F42.wireOp",EDGE,"E53")])]});
            var Q21;
            Q21=makeQuery(id+"F46.opRevolve","SWEPT_BODY",BODY,{"disambiguationData":[OSD([sQuery(id+"F45.wireOp",EDGE,"E54"),sQuery(id+"F45.wireOp",EDGE,"E55"),sQuery(id+"F45.wireOp",EDGE,"E56")])]});
            var Q22;
            Q22=makeQuery(id+"F47.opRevolve","SWEPT_BODY",BODY,{"disambiguationData":[OSD([sQuery(id+"F45.wireOp",EDGE,"E54"),sQuery(id+"F45.wireOp",EDGE,"E55"),sQuery(id+"F45.wireOp",EDGE,"E56")])]});
            var Q23;
            Q23=makeQuery(id+"F49.opRevolve","SWEPT_BODY",BODY,{"disambiguationData":[OSD([sQuery(id+"F48.wireOp",EDGE,"E57"),sQuery(id+"F48.wireOp",EDGE,"E58")])]});
            var Q24;
            Q24=makeQuery(id+"F51.opRevolve","SWEPT_BODY",BODY,{"disambiguationData":[OSD([sQuery(id+"F50.wireOp",EDGE,"E59"),sQuery(id+"F50.wireOp",EDGE,"E60"),sQuery(id+"F50.wireOp",EDGE,"E61")])]});
            var Q25;
            Q25=makeQuery(id+"F52.opRevolve","SWEPT_BODY",BODY,{"disambiguationData":[OSD([sQuery(id+"F50.wireOp",EDGE,"E59"),sQuery(id+"F50.wireOp",EDGE,"E60"),sQuery(id+"F50.wireOp",EDGE,"E61")])]});
            var Q26;
            Q26=makeQuery(id+"F54.opRevolve","SWEPT_BODY",BODY,{"disambiguationData":[OSD([sQuery(id+"F53.wireOp",EDGE,"E62"),sQuery(id+"F53.wireOp",EDGE,"E63"),sQuery(id+"F53.wireOp",EDGE,"E64")])]});
            var Q27;
            Q27=makeQuery(id+"F55.opRevolve","SWEPT_BODY",BODY,{"disambiguationData":[OSD([sQuery(id+"F53.wireOp",EDGE,"E62"),sQuery(id+"F53.wireOp",EDGE,"E63"),sQuery(id+"F53.wireOp",EDGE,"E64")])]});
            var Q28;
            Q28=makeQuery(id+"F57.opRevolve","SWEPT_BODY",BODY,{"disambiguationData":[OSD([sQuery(id+"F56.wireOp",EDGE,"E65"),sQuery(id+"F56.wireOp",EDGE,"E66"),sQuery(id+"F56.wireOp",EDGE,"E67")])]});
            var Q29;
            Q29=makeQuery(id+"F58.opRevolve","SWEPT_BODY",BODY,{"disambiguationData":[OSD([sQuery(id+"F56.wireOp",EDGE,"E65"),sQuery(id+"F56.wireOp",EDGE,"E66"),sQuery(id+"F56.wireOp",EDGE,"E67")])]});
            var Q30;
            Q30=makeQuery(id+"F60.opRevolve","SWEPT_BODY",BODY,{"disambiguationData":[OSD([sQuery(id+"F59.wireOp",EDGE,"E68"),sQuery(id+"F59.wireOp",EDGE,"E69"),sQuery(id+"F59.wireOp",EDGE,"E70")])]});
            var Q31;
            Q31=makeQuery(id+"F61.opRevolve","SWEPT_BODY",BODY,{"disambiguationData":[OSD([sQuery(id+"F59.wireOp",EDGE,"E68"),sQuery(id+"F59.wireOp",EDGE,"E69"),sQuery(id+"F59.wireOp",EDGE,"E70")])]});
            var Q32;
            Q32=makeQuery(id+"F62.opRevolve","SWEPT_BODY",BODY,{"disambiguationData":[OSD([sQuery(id+"F42.wireOp",EDGE,"E50"),sQuery(id+"F42.wireOp",EDGE,"E52"),sQuery(id+"F42.wireOp",EDGE,"E53")])]});
            var Q33;
            Q33=makeQuery(id+"F63.opRevolve","SWEPT_BODY",BODY,{"disambiguationData":[OSD([sQuery(id+"F42.wireOp",EDGE,"E50"),sQuery(id+"F42.wireOp",EDGE,"E52"),sQuery(id+"F42.wireOp",EDGE,"E53")])]});
            var Q34;
            Q34=makeQuery(id+"F64.opRevolve","SWEPT_BODY",BODY,{"disambiguationData":[OSD([sQuery(id+"F0.wireOp",EDGE,"E2"),sQuery(id+"F0.wireOp",EDGE,"E3"),sQuery(id+"F0.wireOp",EDGE,"E4")])]});
            booleanBodies(context, id + "F65", {"operationType" : BooleanOperationType.UNION, "tools" : qUnion([Q0, Q1, Q2, Q3, Q4, Q5, Q6, Q7, Q8, Q9, Q10, Q11, Q12, Q13, Q14, Q15, Q16, Q17, Q18, Q19, Q20, Q21, Q22, Q23, Q24, Q25, Q26, Q27, Q28, Q29, Q30, Q31, Q32, Q33, Q34])});
        }
    });
